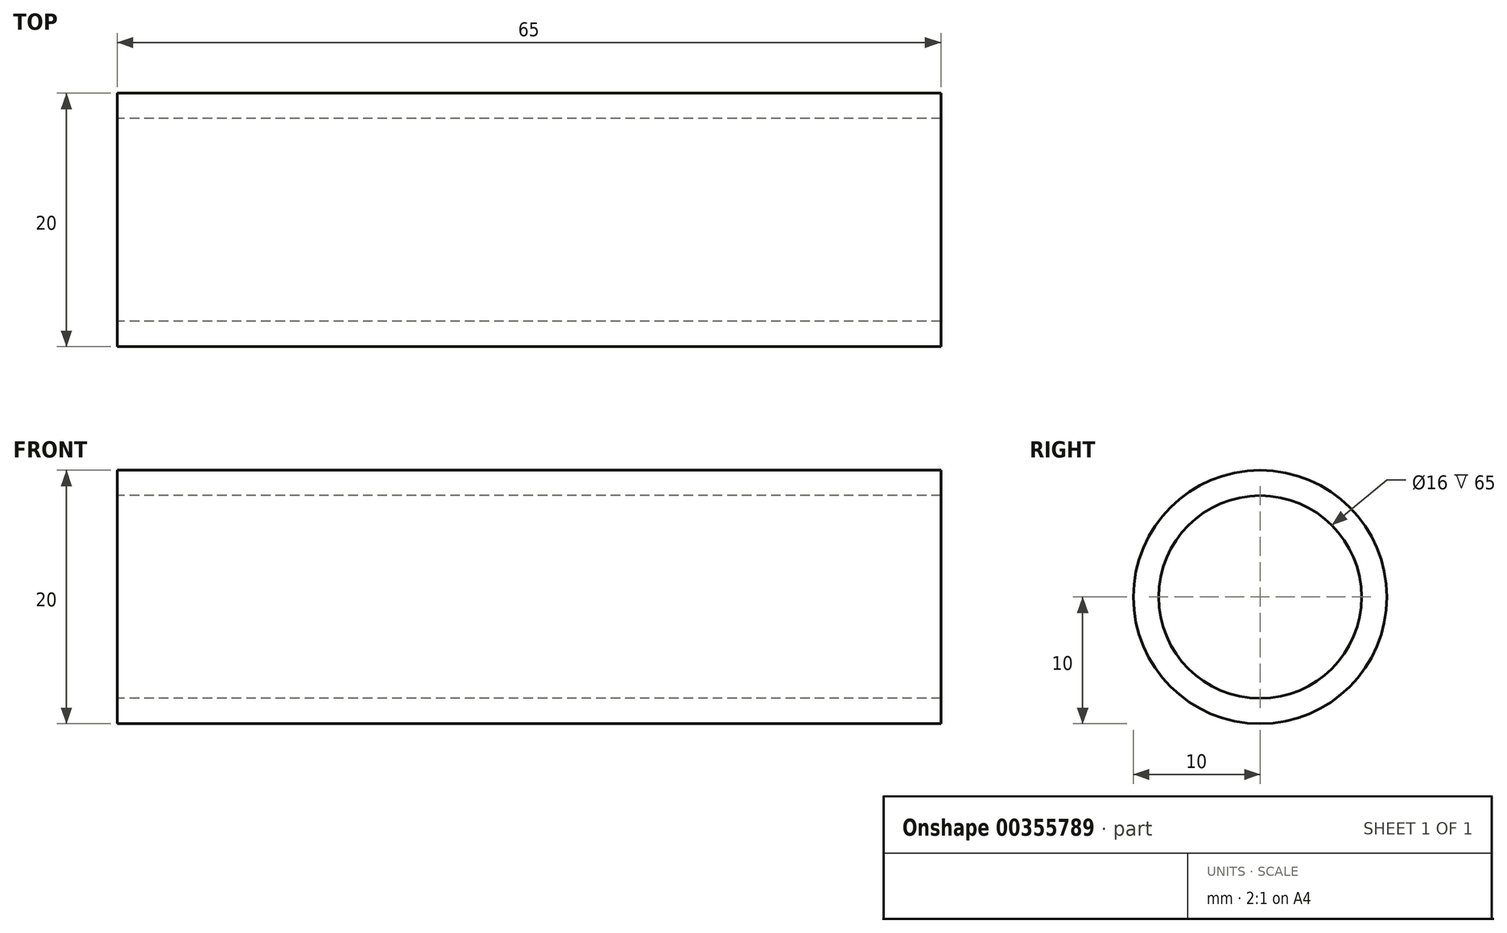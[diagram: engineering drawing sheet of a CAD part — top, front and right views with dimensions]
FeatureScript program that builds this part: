
annotation { "Feature Type Name" : "Feature", "Feature Type Description" : "" }
export const myFeature = defineFeature(function(context is Context, id is Id, definition is map)
    precondition{}
    {
        {
            var Q0;
            Q0=qCreatedBy(makeId("Right.planeOp"),FACE);
            var sketch = newSketch(context, id + "F0", { "sketchPlane" : qUnion([Q0])});
            skCircle(sketch, "E0", {"center": v(0, 0) * mm, "radius": 8 * mm});
            skCircle(sketch, "E1", {"center": v(0, 0) * mm, "radius": 10 * mm});
            skSolve(sketch);
        }
        {
            var Q0;
            Q0=qSketchRegion(id+"F0",true);
            extrude(context, id + "F1", {"entities" : qUnion([Q0]), "depth" : 50 * mm, "hasSecondDirection" : true, "secondDirectionOppositeDirection" : true, "secondDirectionDepth" : 15 * mm});
        }
    });
